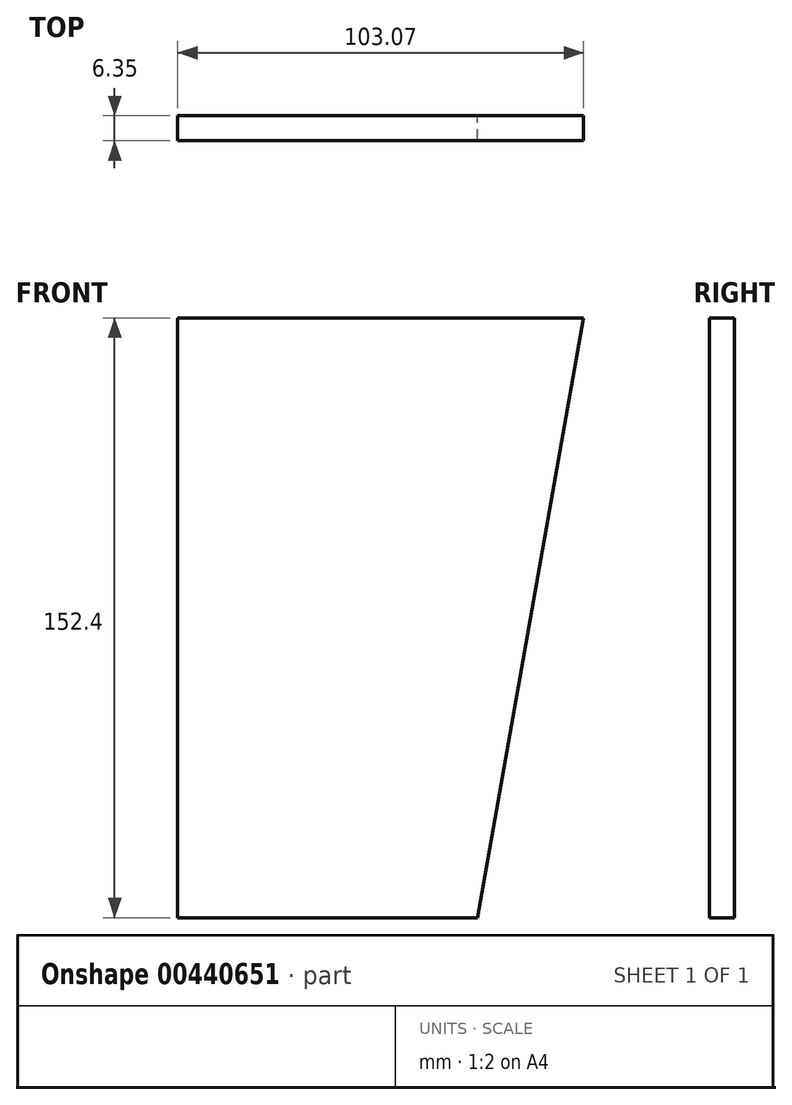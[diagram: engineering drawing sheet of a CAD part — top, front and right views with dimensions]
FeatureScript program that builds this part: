
annotation { "Feature Type Name" : "Feature", "Feature Type Description" : "" }
export const myFeature = defineFeature(function(context is Context, id is Id, definition is map)
    precondition{}
    {
        {
            var Q0;
            Q0=qCreatedBy(makeId("Front.planeOp"),FACE);
            var sketch = newSketch(context, id + "F0", { "sketchPlane" : qUnion([Q0])});
            skLineSegment(sketch, "E0", {"start": v(0, 0) * mm, "end": v(76.2, 0) * mm});
            skLineSegment(sketch, "E1", {"start": v(0, 0) * mm, "end": v(0, 152.4) * mm});
            skLineSegment(sketch, "E2", {"start": v(76.2, 0) * mm, "end": v(103.07, 152.4) * mm});
            skLineSegment(sketch, "E3", {"start": v(0, 152.4) * mm, "end": v(103.07, 152.4) * mm});
            skSolve(sketch);
        }
        {
            var Q0;
            Q0 = qSketchRegion(id + "F0", true);
            extrude(context, id + "F1", {"entities" : qUnion([Q0]), "depth" : 6.35 * mm});
        }
    });
